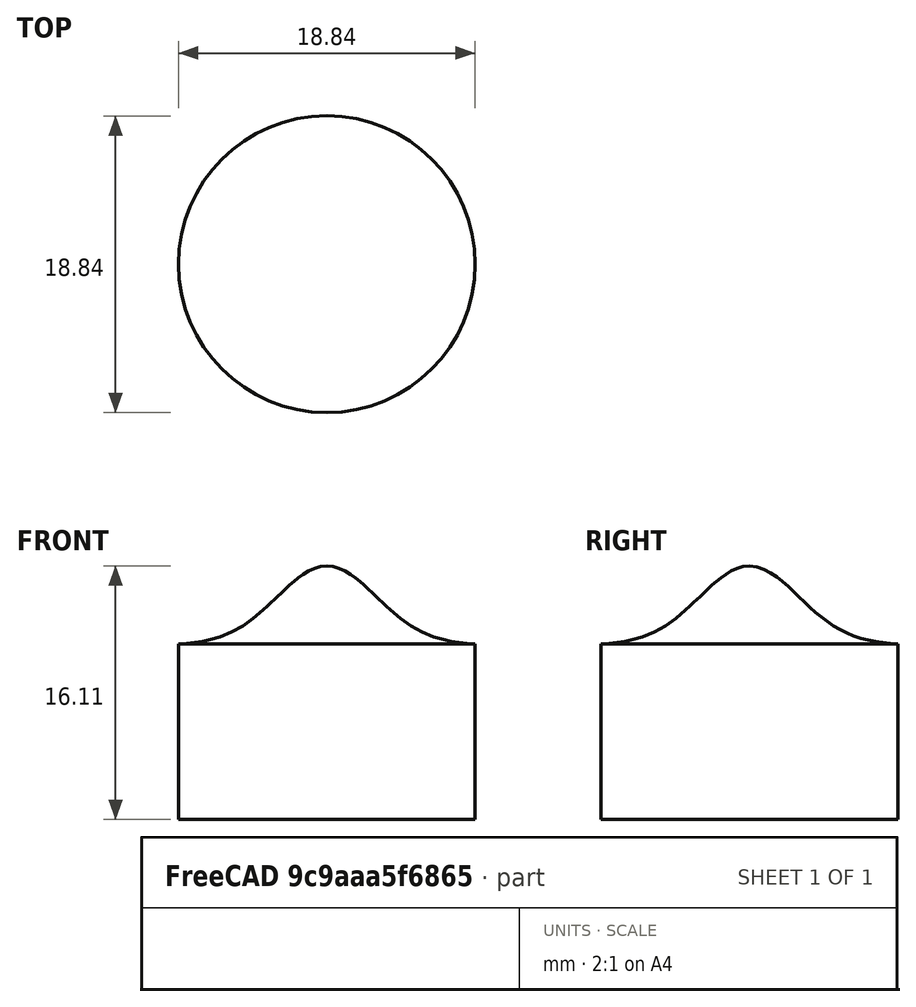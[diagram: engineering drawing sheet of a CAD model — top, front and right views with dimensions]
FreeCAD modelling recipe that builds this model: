
FCSTD DOCUMENT  (FreeCAD 1.0RUnknown)
Label: parametric-curves-gaussian-partWB
License: All rights reserved
LicenseURL: https://en.wikipedia.org/wiki/All_rights_reserved
objects: Part::Revolution×2, Part::FeaturePython×1, Sketcher::SketchObject×1
note: 5 computed .brp shape members not serialized (recipe doc carries the construction recipe); baked Part::Feature solids carry a one-line shape summary decoded from their .brp

FEATURE [Part::FeaturePython] ParametricCurve  # WARN: FeaturePython — macro-defined, semantics opaque (R4)
  AttacherType = Attacher::AttachEngine3D
  Closed = false
  Continuity = C2
  EditFormulas = false
  F_X = 0
  F_Y = 0
  F_Z = 0
  F_a = 0
  F_b = 0
  F_c = 0
  F_d = [0,0]
  FormulaName = formula1
  Formulas = 0
  Interval = 0.1
  MakeFace = false
  PlusOneIteration = true
  Points = (96) [(0,0,5),(0,0.1,4.9975),(0,0.2,4.99001),(0,0.3,4.97755),(0,0.4,4.96016),(0,0.5,4.93789),(0,0.6,4.91081),(0,0.7,4.87899),(0,0.8,4.84253),+87 more]
  ShapeType = 0
  Sorted = false
  UpdateSpreadsheet = false
  UseSpreadsheet = false
  Version = 2025.05.08
  X = 0
  Y = t
  Z = 5*exp(-0.05*t*t)
  t_max = 9.42478
  t_min = 0
FEATURE [Sketcher::SketchObject] Sketch
  ArcFitTolerance = 1e-06
  ExternalGeometry = -> [ParametricCurve]
  FullyConstrained = false
  MakeInternals = false
  Placement = pos=(0,0,0) rot=(0.57735,0.57735,0.57735;2.0944rad)
  sketch-geometry (3):
    g0: LineSegment StartX=0 StartY=5 StartZ=0 EndX=0 EndY=-11.1092 EndZ=0
    g1: LineSegment StartX=0 StartY=-11.1092 StartZ=0 EndX=9.42478 EndY=-11.1092 EndZ=0
    g2: LineSegment StartX=9.42478 StartY=-11.1092 StartZ=0 EndX=9.42478 EndY=0.0589018 EndZ=0
  constraints (7):
    c: Coincident(g0,g-3)
    c: PointOnObject(g0,g-2)
    c: Coincident(g0,g1)
    c: Horizontal(g1)
    c: Coincident(g1,g2)
    c: Coincident(g2,g-3)
    c: Vertical(g2)
FEATURE [Part::Revolution] Revolve
  Angle = 360
  Axis = (0,0,1)
  Base = (0,0,0)
  FaceMakerClass = Part::FaceMakerBullseye
  Solid = false
  Source = -> ParametricCurve
  Symmetric = false
FEATURE [Part::Revolution] Revolve001
  Angle = 360
  Axis = (0,0,1)
  Base = (0,0,0)
  FaceMakerClass = Part::FaceMakerBullseye
  Solid = false
  Source = -> Sketch
  Symmetric = false
